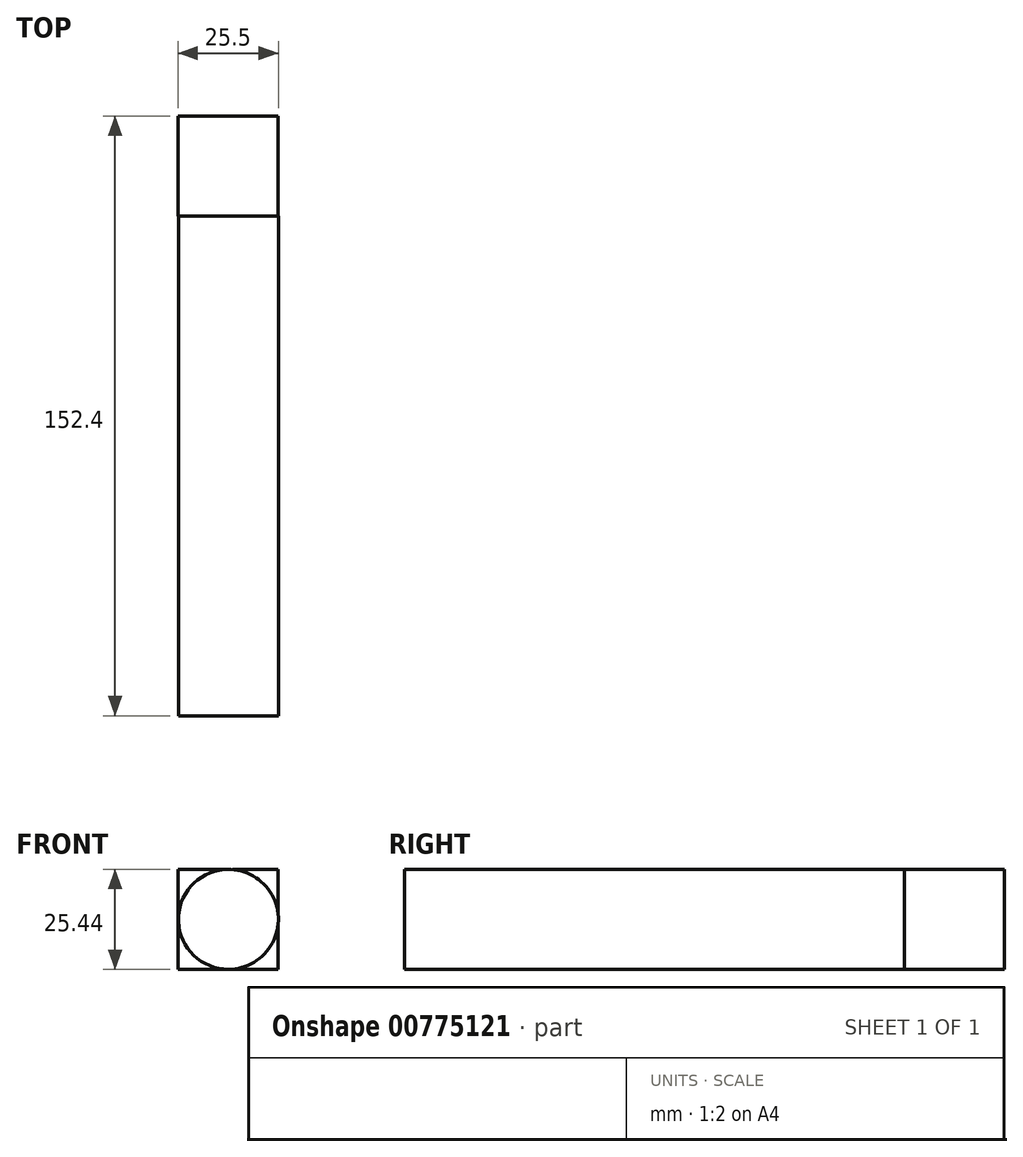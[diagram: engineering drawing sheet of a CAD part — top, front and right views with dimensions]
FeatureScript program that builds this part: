
annotation { "Feature Type Name" : "Feature", "Feature Type Description" : "" }
export const myFeature = defineFeature(function(context is Context, id is Id, definition is map)
    precondition{}
    {
        {
            var Q0;
            Q0=qCreatedBy(makeId("Front.planeOp"),FACE);
            var sketch = newSketch(context, id + "F0", { "sketchPlane" : qUnion([Q0])});
            skCircle(sketch, "E0", {"center": v(48.14, 27.8) * mm, "radius": 12.7 * mm});
            skSolve(sketch);
        }
        {
            var Q0;
            Q0=makeQuery(id+"F0.imprint","IMPRINT",FACE,{"disambiguationData":[TD([[makeQuery(id+"F0.imprint","IMPRINT",EDGE,{"derivedFrom":sQuery(id+"F0.wireOp",EDGE,"E0")}),1.0]])]});
            extrude(context, id + "F1", {"entities" : qUnion([Q0]), "depth" : 127 * mm, "offsetDistance" : 25.4 * mm});
        }
        {
            var Q0;
            Q0=makeQuery(id+"F1.opExtrude","CAP_FACE",FACE,{"disambiguationData":[OSD([sQuery(id+"F0.wireOp",EDGE,"E0")])],"isStart":true});
            var sketch = newSketch(context, id + "F2", { "sketchPlane" : qUnion([Q0])});
            skLineSegment(sketch, "E1.bottom", {"start": v(-60.74, 40.46) * mm, "end": v(-35.34, 40.46) * mm});
            skLineSegment(sketch, "E1.top", {"start": v(-60.74, 15.06) * mm, "end": v(-35.34, 15.06) * mm});
            skLineSegment(sketch, "E1.left", {"start": v(-60.74, 40.46) * mm, "end": v(-60.74, 15.06) * mm});
            skLineSegment(sketch, "E1.right", {"start": v(-35.34, 40.46) * mm, "end": v(-35.34, 15.06) * mm});
            skSolve(sketch);
        }
        {
            var Q0;
            Q0=makeQuery(id+"F1.opExtrude","CAP_FACE",FACE,{"disambiguationData":[OSD([sQuery(id+"F0.wireOp",EDGE,"E0")])],"isStart":false});
            var sketch = newSketch(context, id + "F3", { "sketchPlane" : qUnion([Q0])});
            skLineSegment(sketch, "E2.bottom", {"start": v(35.42, 40.54) * mm, "end": v(60.82, 40.54) * mm});
            skLineSegment(sketch, "E2.top", {"start": v(35.42, 15.14) * mm, "end": v(60.82, 15.14) * mm});
            skLineSegment(sketch, "E2.left", {"start": v(35.42, 40.54) * mm, "end": v(35.42, 15.14) * mm});
            skLineSegment(sketch, "E2.right", {"start": v(60.82, 40.54) * mm, "end": v(60.82, 15.14) * mm});
            skSolve(sketch);
        }
        {
            var Q0;
            Q0=sQuery(id+"F3.wireOp",EDGE,"E2.left");
            var Q1;
            Q1=sQuery(id+"F3.wireOp",EDGE,"E2.top");
            var Q2;
            Q2=sQuery(id+"F3.wireOp",EDGE,"E2.right");
            var Q3;
            Q3=sQuery(id+"F3.wireOp",EDGE,"E2.bottom");
            extrude(context, id + "F4", {"bodyType" : ToolBodyType.SURFACE, "surfaceEntities" : qUnion([Q0, Q1, Q2, Q3]), "oppositeDirection" : true, "depth" : 25.4 * mm, "offsetDistance" : 25.4 * mm});
        }
        {
            var Q0;
            {var subQ0=sQuery(id+"F2.wireOp",EDGE,"E1.left");var subQ1=sQuery(id+"F2.wireOp",EDGE,"E1.bottom");var subQ2=makeQuery(id+"F2.imprint","INTERSECT",VERTEX,{"derivedFrom":[subQ1,subQ0]});Q0=makeQuery(id+"F2.imprint","IMPRINT",FACE,{"disambiguationData":[TD([[makeQuery(id+"F2.imprint","IMPRINT",EDGE,{"disambiguationData":[TD([[subQ2,-1.0]])],"derivedFrom":subQ1}),-1.0]])]});}
            var Q1;
            {var subQ1=sQuery(id+"F2.wireOp",EDGE,"E1.top");Q1=makeQuery(id+"F2.imprint","IMPRINT",FACE,{"disambiguationData":[TD([[makeQuery(id+"F2.imprint","IMPRINT",EDGE,{"derivedFrom":subQ1}),1.0]])]});}
            var Q2;
            {var subQ0=sQuery(id+"F2.wireOp",EDGE,"E1.bottom");var subQ1=makeQuery(id+"F1.opExtrude","CAP_EDGE",EDGE,{"disambiguationData":[OSD([sQuery(id+"F0.wireOp",EDGE,"E0")])],"isStart":true});var subQ2=makeQuery(id+"F2.imprint","INTERSECT",VERTEX,{"disambiguationData":[OD(0.0)],"derivedFrom":[subQ1,subQ0]});Q2=makeQuery(id+"F2.imprint","IMPRINT",FACE,{"disambiguationData":[TD([[makeQuery(id+"F2.imprint","IMPRINT",EDGE,{"disambiguationData":[TD([[subQ2,-1.0]])],"derivedFrom":subQ0}),-1.0]])]});}
            extrude(context, id + "F5", {"entities" : qUnion([Q0, Q1, Q2]), "operationType" : NewBodyOperationType.ADD, "depth" : 25.4 * mm, "offsetDistance" : 25.4 * mm});
        }
    });
